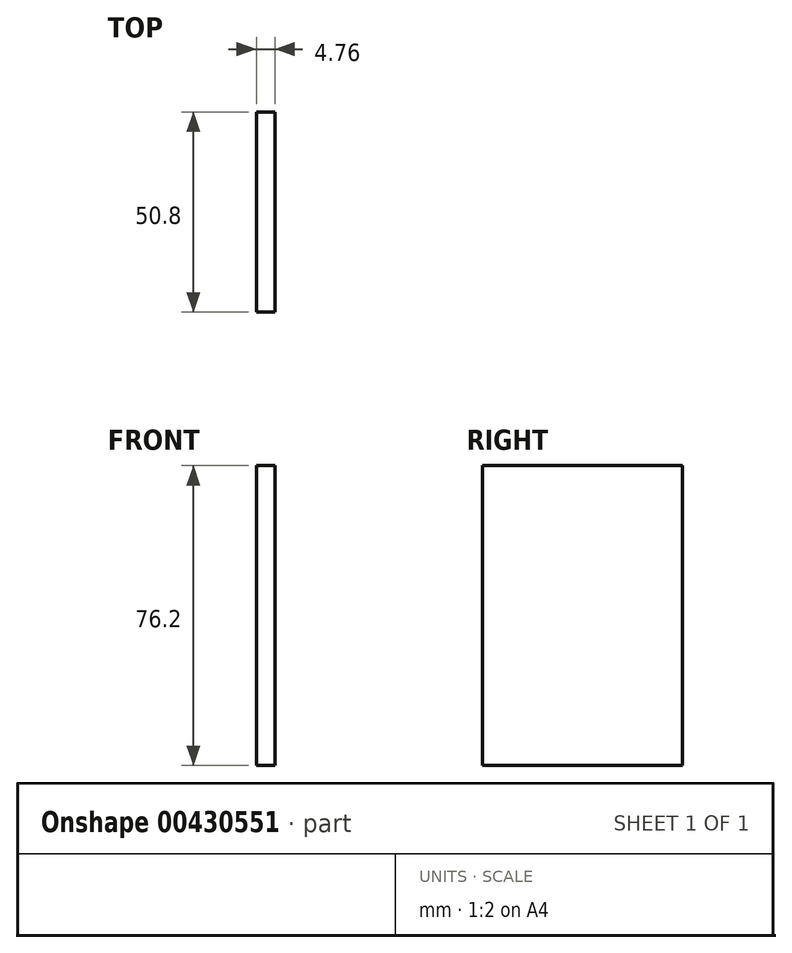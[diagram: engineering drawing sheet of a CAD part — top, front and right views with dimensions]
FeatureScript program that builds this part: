
annotation { "Feature Type Name" : "Feature", "Feature Type Description" : "" }
export const myFeature = defineFeature(function(context is Context, id is Id, definition is map)
    precondition{}
    {
        {
            var Q0;
            Q0=qCreatedBy(makeId("Right.planeOp"),FACE);
            var sketch = newSketch(context, id + "F0", { "sketchPlane" : qUnion([Q0])});
            skLineSegment(sketch, "E0.bottom", {"start": v(-45.36, 42.05) * mm, "end": v(5.44, 42.05) * mm});
            skLineSegment(sketch, "E0.top", {"start": v(-45.36, -34.15) * mm, "end": v(5.44, -34.15) * mm});
            skLineSegment(sketch, "E0.left", {"start": v(-45.36, 42.05) * mm, "end": v(-45.36, -34.15) * mm});
            skLineSegment(sketch, "E0.right", {"start": v(5.44, 42.05) * mm, "end": v(5.44, -34.15) * mm});
            skSolve(sketch);
        }
        {
            var Q0;
            Q0=makeQuery(id+"F0.imprint","IMPRINT",FACE,{"disambiguationData":[TD([[makeQuery(id+"F0.imprint","IMPRINT",EDGE,{"derivedFrom":sQuery(id+"F0.wireOp",EDGE,"E0.bottom")}),-1.0]])]});
            extrude(context, id + "F1", {"entities" : qUnion([Q0]), "depth" : 4.76 * mm});
        }
    });
